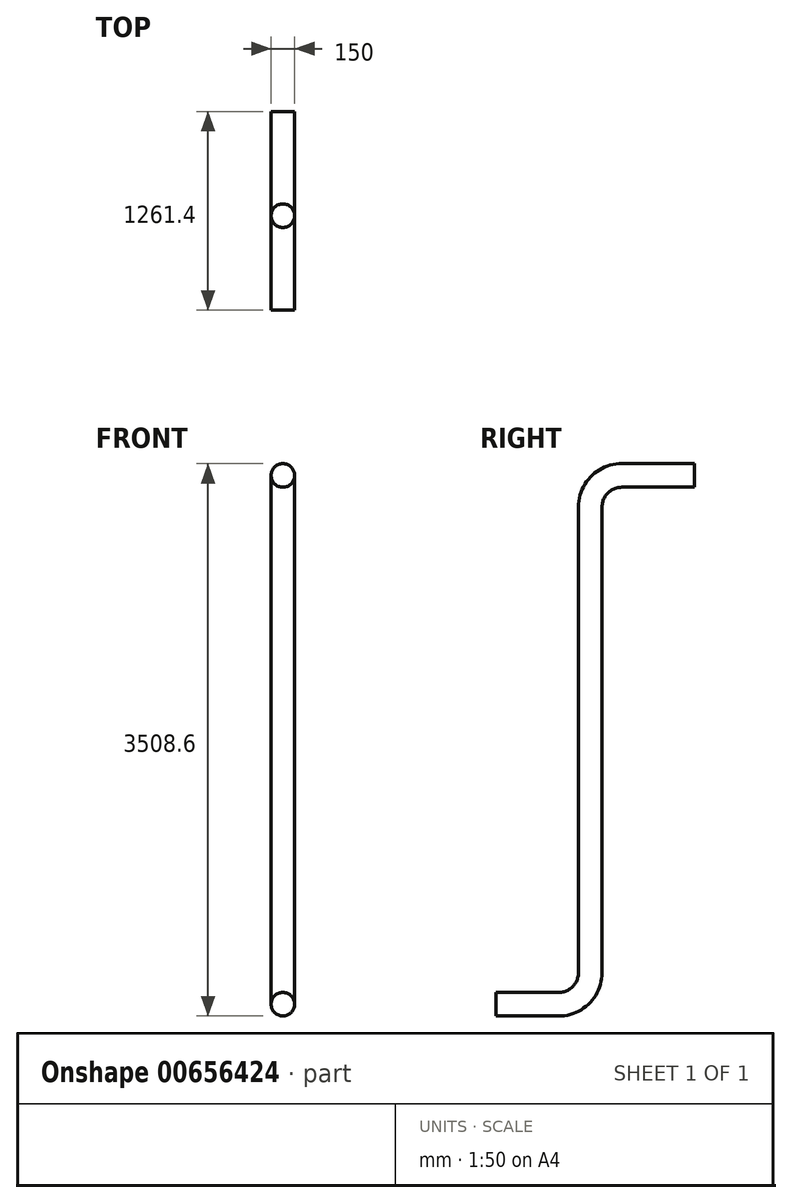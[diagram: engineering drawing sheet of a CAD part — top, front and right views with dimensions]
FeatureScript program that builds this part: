
annotation { "Feature Type Name" : "Feature", "Feature Type Description" : "" }
export const myFeature = defineFeature(function(context is Context, id is Id, definition is map)
    precondition{}
    {
        {
            var Q0;
            Q0=qCreatedBy(makeId("Right.planeOp"),FACE);
            var sketch = newSketch(context, id + "F0", { "sketchPlane" : qUnion([Q0])});
            skLineSegment(sketch, "E0", {"start": v(0, 0) * mm, "end": v(400, 0) * mm});
            skLineSegment(sketch, "E1", {"start": v(600, 200) * mm, "end": v(600, 3158.6) * mm});
            skLineSegment(sketch, "E2", {"start": v(800, 3358.6) * mm, "end": v(1261.4, 3358.6) * mm});
            skPoint(sketch, "E3.visualSharp", {"position": v(600, 3358.6) * mm});
            skArc(sketch, "E3.filletArc", {"start": v(800, 3358.6) * mm, "mid": v(658.58, 3300.02) * mm, "end": v(600, 3158.6) * mm});
            skPoint(sketch, "E4.visualSharp", {"position": v(600, 0) * mm});
            skArc(sketch, "E4.filletArc", {"start": v(400, 0) * mm, "mid": v(541.42, 58.58) * mm, "end": v(600, 200) * mm});
            skSolve(sketch);
        }
        {
            var Q0;
            Q0=qCreatedBy(makeId("Front.planeOp"),FACE);
            var sketch = newSketch(context, id + "F1", { "sketchPlane" : qUnion([Q0])});
            skCircle(sketch, "E5", {"center": v(0, 0) * mm, "radius": 75 * mm});
            skSolve(sketch);
        }
        {
            var Q0;
            Q0=makeQuery(id+"F1.imprint","IMPRINT",FACE,{"disambiguationData":[TD([[makeQuery(id+"F1.imprint","IMPRINT",EDGE,{"derivedFrom":sQuery(id+"F1.wireOp",EDGE,"E5")}),1.0]])]});
            var Q1;
            Q1=sQuery(id+"F0.wireOp",EDGE,"E0");
            var Q2;
            Q2=sQuery(id+"F0.wireOp",EDGE,"E4.filletArc");
            var Q3;
            Q3=sQuery(id+"F0.wireOp",EDGE,"E1");
            var Q4;
            Q4=sQuery(id+"F0.wireOp",EDGE,"E3.filletArc");
            var Q5;
            Q5=sQuery(id+"F0.wireOp",EDGE,"E2");
            sweep(context, id + "F2", {"profiles" : qUnion([Q0]), "path" : qUnion([Q1, Q2, Q3, Q4, Q5])});
        }
    });
